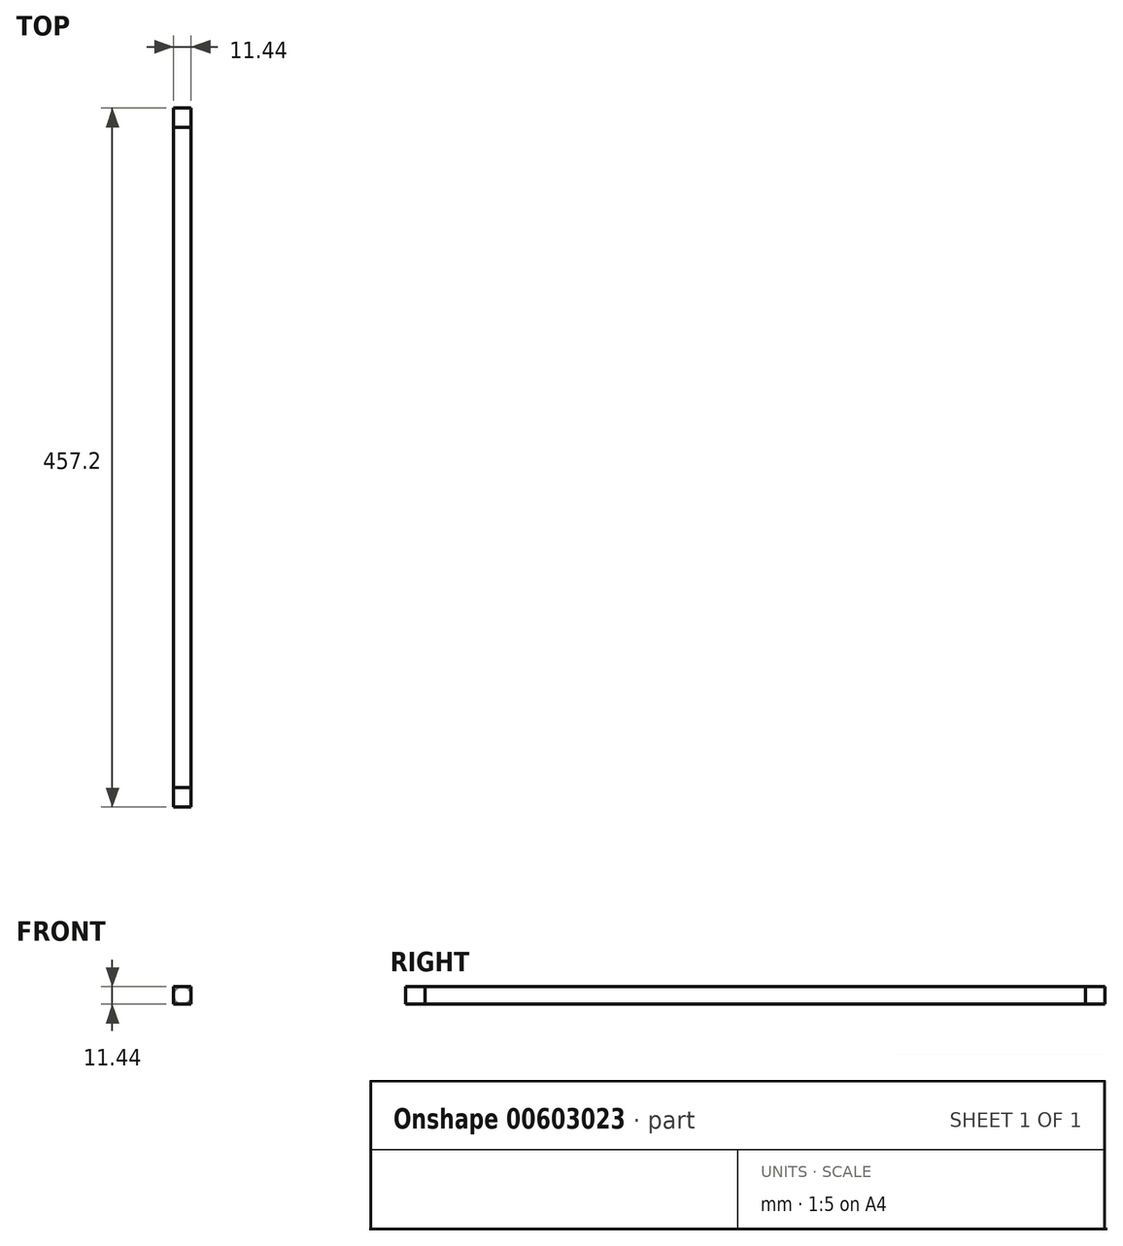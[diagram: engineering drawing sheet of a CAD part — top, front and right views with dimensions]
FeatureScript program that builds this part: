
annotation { "Feature Type Name" : "Feature", "Feature Type Description" : "" }
export const myFeature = defineFeature(function(context is Context, id is Id, definition is map)
    precondition{}
    {
        {
            var Q0;
            Q0=qCreatedBy(makeId("Front.planeOp"),FACE);
            var sketch = newSketch(context, id + "F0", { "sketchPlane" : qUnion([Q0])});
            skCircle(sketch, "E0", {"center": v(0, 0) * mm, "radius": 5.72 * mm});
            skSolve(sketch);
        }
        {
            var Q0;
            Q0 = qSketchRegion(id + "F0", true);
            extrude(context, id + "F1", {"entities" : qUnion([Q0]), "depth" : 457.2 * mm, "offsetDistance" : 25.4 * mm});
        }
        {
            var Q0;
            Q0=makeQuery(id+"F1.opExtrude","CAP_FACE",FACE,{"disambiguationData":[OSD([sQuery(id+"F0.wireOp",EDGE,"E0")])],"isStart":false});
            var sketch = newSketch(context, id + "F2", { "sketchPlane" : qUnion([Q0])});
            skLineSegment(sketch, "E1.bottom", {"start": v(5.72, -5.71) * mm, "end": v(-5.72, -5.72) * mm});
            skLineSegment(sketch, "E1.top", {"start": v(5.72, 5.72) * mm, "end": v(-5.72, 5.71) * mm});
            skLineSegment(sketch, "E1.left", {"start": v(5.72, -5.71) * mm, "end": v(5.72, 5.72) * mm});
            skLineSegment(sketch, "E1.right", {"start": v(-5.72, -5.72) * mm, "end": v(-5.72, 5.71) * mm});
            skPoint(sketch, "E1.middle", {"position": v(0, 0) * mm});
            skSolve(sketch);
        }
        {
            var Q0;
            Q0 = qSketchRegion(id + "F2", true);
            extrude(context, id + "F3", {"entities" : qUnion([Q0]), "operationType" : NewBodyOperationType.ADD, "oppositeDirection" : true, "depth" : 12.7 * mm, "offsetDistance" : 25.4 * mm});
        }
        {
            var Q0;
            Q0=makeQuery(id+"F1.opExtrude","CAP_FACE",FACE,{"disambiguationData":[OSD([sQuery(id+"F0.wireOp",EDGE,"E0")])],"isStart":true});
            var sketch = newSketch(context, id + "F4", { "sketchPlane" : qUnion([Q0])});
            skLineSegment(sketch, "E2.bottom", {"start": v(5.72, -5.71) * mm, "end": v(-5.72, -5.72) * mm});
            skLineSegment(sketch, "E2.top", {"start": v(5.72, 5.72) * mm, "end": v(-5.72, 5.71) * mm});
            skLineSegment(sketch, "E2.left", {"start": v(5.72, -5.71) * mm, "end": v(5.72, 5.72) * mm});
            skLineSegment(sketch, "E2.right", {"start": v(-5.72, -5.72) * mm, "end": v(-5.72, 5.71) * mm});
            skPoint(sketch, "E2.middle", {"position": v(0, 0) * mm});
            skSolve(sketch);
        }
        {
            var Q0;
            Q0 = qSketchRegion(id + "F4", true);
            extrude(context, id + "F5", {"entities" : qUnion([Q0]), "operationType" : NewBodyOperationType.ADD, "oppositeDirection" : true, "depth" : 12.7 * mm, "offsetDistance" : 25.4 * mm});
        }
    });
